# Revit family: MTXTYP003
name_source: partatom
category: Furniture
units: mm (PartAtom-declared; Revit-internal decimal feet)

## family parameters
Always vertical = Yes
Cut with Voids When Loaded = No
OmniClass Number = 23.40.20.00
OmniClass Title = General Furniture and Specialties
Render Appearance Source = Family Geometry
Room Calculation Point = No
Shared = No
Work Plane-Based = No

## types (1)
- MTXTYP003
    Cost = 69702 $
    Default Elevation = 0 mm  [stored 0 ft]
    Description = 1 x 57 in. Electrical Jumper  (Pt 36E & Vt 48), 3 x Matrix White Duplex Outlet - Line 1, 3 x Matrix White Duplex Outlet - Line 2, 3 x Matrix White Duplex Outlet - Line 3, 3 x Matrix White Duplex Outlet - Line 4 - Dedicated, 1 x 18 in. Electrical Jumper  (Panel To Panel), 1 x 21 in. Electrical Jumper  (Extended Panel To Panel), 4 x Single Powerway Assembly - 36W - 8 wire, 4 circuit, 6 x Access Hole Cover, 1 x LH Receptacle Mounted Base Infeed - 72L - 8 Wire, 4 Circuit, 1 x Dual Electrical Tile - 8H X 36W, 11 x Quad Electrical Tile - 8H X 36W, 12 x Tackable Acoustical Tile - 40H x 36W, 3 x MATRIX LINEAR Double Frame Recessed Glass Kit 36" & 36", 6 x Panel Frame - Linear Trim - 50H x 36W, 2 x MTX Gallery Panel EOR DBL-50H x 90W Horz, 2 x MTX Gallery Panel Spine DBL-50H x 90W Horz, 3 x MATRIX RECESSED FRAMELESS GLASS 12"H X 72"W V2, 6 x Pedestal - B/B/F - 24D, 6 x PEDESTAL LSERIES BOX/FILE MOBILE 24" WITH CUSHION, 6 x Silver Key Alike Kit (2 Cores) - Wesko Type, 6 x TBL, REC, 2mm, 30Dx48Wx29H, HAL, E SERIES GLD 2 STAGE, 6 x Rectangular - 2mm Edge - 24D x 72W, 6 x Regular Cantilever - Left Hand - 24D, 6 x Regular Cantilever - Right Hand - 24D, 3 x Lite Clip Scrn,LWrp PM,PET,Dim J,UMnt,LH,26hx30dx48w, 3 x Lite Clip Scrn,LWrp PM,PET,Dim J,UMnt,RH,26hx30dx48w
    Exported From CET Designer = Yes
    Manufacturer = AIS
    Model = E-MW8W4PJ36E
    Show MTXTYP003 = Yes
    VisibilityIndex = 0

note: [stored X ft] marks values corroborated as IEEE doubles in the binary element streams (Revit-internal decimal feet)

## geometry (parser evidence)
native form markers: Sweep x2
no freeform markers — native parametric forms only
